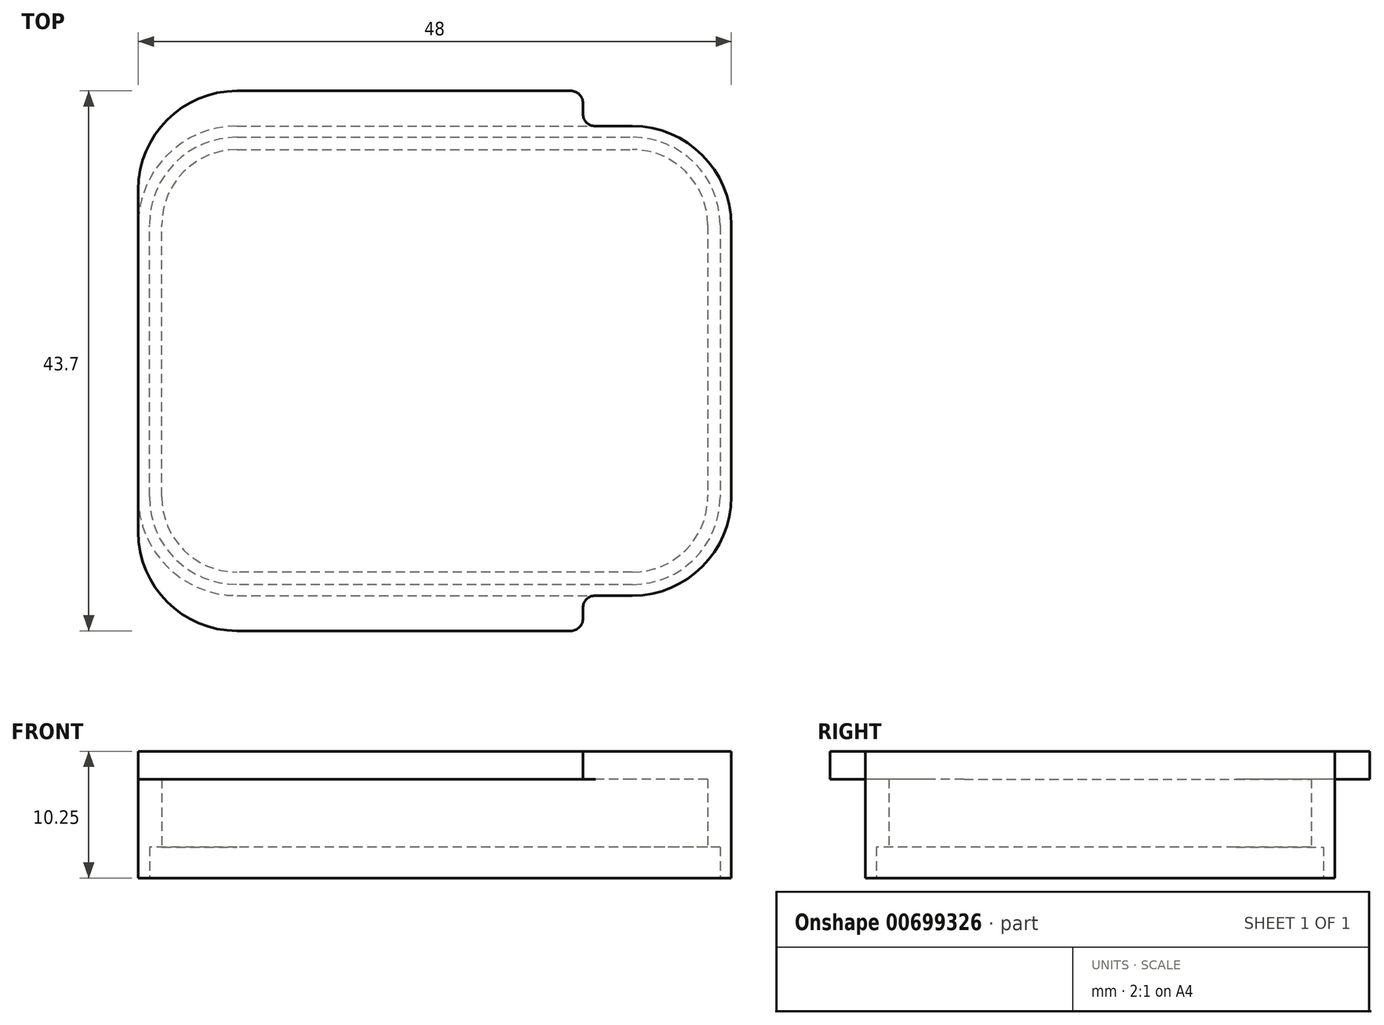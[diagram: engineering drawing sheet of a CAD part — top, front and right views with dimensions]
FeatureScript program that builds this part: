
annotation { "Feature Type Name" : "Feature", "Feature Type Description" : "" }
export const myFeature = defineFeature(function(context is Context, id is Id, definition is map)
    precondition{}
    {
        {
            var Q0;
            Q0=qCreatedBy(makeId("Top.planeOp"),FACE);
            var sketch = newSketch(context, id + "F0", { "sketchPlane" : qUnion([Q0])});
            skLineSegment(sketch, "E0.bottom", {"start": v(-16, 19) * mm, "end": v(16, 19) * mm});
            skLineSegment(sketch, "E0.top", {"start": v(-16, -19) * mm, "end": v(16, -19) * mm});
            skLineSegment(sketch, "E0.left", {"start": v(-24, 11) * mm, "end": v(-24, -11) * mm});
            skLineSegment(sketch, "E0.right", {"start": v(24, 11) * mm, "end": v(24, -11) * mm});
            skPoint(sketch, "E1.visualSharp", {"position": v(-24, 19) * mm});
            skArc(sketch, "E1.filletArc", {"start": v(-16, 19) * mm, "mid": v(-21.66, 16.66) * mm, "end": v(-24, 11) * mm});
            skPoint(sketch, "E2.visualSharp", {"position": v(24, 19) * mm});
            skArc(sketch, "E2.filletArc", {"start": v(24, 11) * mm, "mid": v(21.66, 16.66) * mm, "end": v(16, 19) * mm});
            skPoint(sketch, "E3.visualSharp", {"position": v(24, -19) * mm});
            skArc(sketch, "E3.filletArc", {"start": v(16, -19) * mm, "mid": v(21.66, -16.66) * mm, "end": v(24, -11) * mm});
            skPoint(sketch, "E4.visualSharp", {"position": v(-24, -19) * mm});
            skArc(sketch, "E4.filletArc", {"start": v(-24, -11) * mm, "mid": v(-21.66, -16.66) * mm, "end": v(-16, -19) * mm});
            skSolve(sketch);
        }
        {
            var Q0;
            Q0 = qSketchRegion(id + "F0", true);
            extrude(context, id + "F1", {"entities" : qUnion([Q0]), "depth" : 10.25 * mm, "offsetDistance" : 25 * mm});
        }
        {
            var Q0;
            Q0=makeQuery(id+"F1.opExtrude","CAP_FACE",FACE,{"disambiguationData":[OSD([sQuery(id+"F0.wireOp",EDGE,"E0.bottom"),sQuery(id+"F0.wireOp",EDGE,"E0.top"),sQuery(id+"F0.wireOp",EDGE,"E0.left"),sQuery(id+"F0.wireOp",EDGE,"E0.right"),sQuery(id+"F0.wireOp",EDGE,"E1.filletArc"),sQuery(id+"F0.wireOp",EDGE,"E2.filletArc"),sQuery(id+"F0.wireOp",EDGE,"E3.filletArc"),sQuery(id+"F0.wireOp",EDGE,"E4.filletArc")])],"isStart":false});
            var sketch = newSketch(context, id + "F2", { "sketchPlane" : qUnion([Q0])});
            skLineSegment(sketch, "E5.bottom", {"start": v(12, 21.85) * mm, "end": v(-24, 21.85) * mm});
            skLineSegment(sketch, "E5.top", {"start": v(12, -21.85) * mm, "end": v(-24, -21.85) * mm});
            skLineSegment(sketch, "E5.left", {"start": v(12, 21.85) * mm, "end": v(12, -21.85) * mm});
            skLineSegment(sketch, "E5.right", {"start": v(-24, 21.85) * mm, "end": v(-24, -21.85) * mm});
            skSolve(sketch);
        }
        {
            var Q0;
            Q0 = qSketchRegion(id + "F2", true);
            extrude(context, id + "F3", {"entities" : qUnion([Q0]), "operationType" : NewBodyOperationType.ADD, "oppositeDirection" : true, "depth" : 2.25 * mm, "offsetDistance" : 25 * mm});
        }
        {
            var Q0;
            Q0=makeQuery(id+"F3.opExtrude","SWEPT_EDGE",EDGE,{"disambiguationData":[OSD([sQuery(id+"F2.wireOp",EDGE,"E5.top"),sQuery(id+"F2.wireOp",EDGE,"E5.right")])]});
            var Q1;
            Q1=makeQuery(id+"F3.opExtrude","SWEPT_EDGE",EDGE,{"disambiguationData":[OSD([sQuery(id+"F2.wireOp",EDGE,"E5.bottom"),sQuery(id+"F2.wireOp",EDGE,"E5.right")])]});
            fillet(context, id + "F4", {"entities" : qUnion([Q0, Q1]), "radius" : 8 * mm, "tangentPropagation" : true, "allowEdgeOverflow" : false});
        }
        {
            var Q0;
            Q0=makeQuery(id+"F3.opExtrude","SWEPT_EDGE",EDGE,{"disambiguationData":[OSD([sQuery(id+"F2.wireOp",EDGE,"E5.top"),sQuery(id+"F2.wireOp",EDGE,"E5.left")])]});
            var Q1;
            Q1=makeQuery(id+"F3.opExtrude","SWEPT_EDGE",EDGE,{"disambiguationData":[OSD([sQuery(id+"F2.wireOp",EDGE,"E5.bottom"),sQuery(id+"F2.wireOp",EDGE,"E5.left")])]});
            fillet(context, id + "F5", {"entities" : qUnion([Q0, Q1]), "radius" : 1 * mm, "tangentPropagation" : true, "allowEdgeOverflow" : false});
        }
        {
            var Q0;
            Q0=makeQuery(id+"F3.boolean.opBoolean","INTERSECT",EDGE,{"derivedFrom":[makeQuery(id+"F1.opExtrude","SWEPT_FACE",FACE,{"disambiguationData":[OSD([sQuery(id+"F0.wireOp",EDGE,"E0.bottom")])]}),makeQuery(id+"F3.opExtrude","SWEPT_FACE",FACE,{"disambiguationData":[OSD([sQuery(id+"F2.wireOp",EDGE,"E5.left")])]})]});
            var Q1;
            Q1=makeQuery(id+"F3.boolean.opBoolean","INTERSECT",EDGE,{"derivedFrom":[makeQuery(id+"F1.opExtrude","SWEPT_FACE",FACE,{"disambiguationData":[OSD([sQuery(id+"F0.wireOp",EDGE,"E0.top")])]}),makeQuery(id+"F3.opExtrude","SWEPT_FACE",FACE,{"disambiguationData":[OSD([sQuery(id+"F2.wireOp",EDGE,"E5.left")])]})]});
            fillet(context, id + "F6", {"entities" : qUnion([Q0, Q1]), "radius" : 1 * mm, "tangentPropagation" : true, "allowEdgeOverflow" : false});
        }
        {
            var Q0;
            Q0=makeQuery(id+"F1.opExtrude","CAP_FACE",FACE,{"disambiguationData":[OSD([sQuery(id+"F0.wireOp",EDGE,"E0.bottom"),sQuery(id+"F0.wireOp",EDGE,"E0.top"),sQuery(id+"F0.wireOp",EDGE,"E0.left"),sQuery(id+"F0.wireOp",EDGE,"E0.right"),sQuery(id+"F0.wireOp",EDGE,"E1.filletArc"),sQuery(id+"F0.wireOp",EDGE,"E2.filletArc"),sQuery(id+"F0.wireOp",EDGE,"E3.filletArc"),sQuery(id+"F0.wireOp",EDGE,"E4.filletArc")])],"isStart":true});
            var sketch = newSketch(context, id + "F7", { "sketchPlane" : qUnion([Q0])});
            skArc(sketch, "E6.0.0", {"start": v(-16, 19) * mm, "mid": v(-21.66, 16.66) * mm, "end": v(-24, 11) * mm, "construction": true});
            skLineSegment(sketch, "E6.0.1", {"start": v(-24, 11) * mm, "end": v(-24, -11) * mm, "construction": true});
            skArc(sketch, "E6.0.2", {"start": v(-24, -11) * mm, "mid": v(-21.66, -16.66) * mm, "end": v(-16, -19) * mm, "construction": true});
            skLineSegment(sketch, "E6.0.3", {"start": v(-16, -19) * mm, "end": v(16, -19) * mm, "construction": true});
            skArc(sketch, "E6.0.4", {"start": v(16, -19) * mm, "mid": v(21.66, -16.66) * mm, "end": v(24, -11) * mm, "construction": true});
            skLineSegment(sketch, "E6.0.5", {"start": v(24, -11) * mm, "end": v(24, 11) * mm, "construction": true});
            skArc(sketch, "E6.0.6", {"start": v(24, 11) * mm, "mid": v(21.66, 16.66) * mm, "end": v(16, 19) * mm, "construction": true});
            skLineSegment(sketch, "E6.0.7", {"start": v(16, 19) * mm, "end": v(-16, 19) * mm, "construction": true});
            skArc(sketch, "E7.0", {"start": v(23.1, 11) * mm, "mid": v(21.02, 16.02) * mm, "end": v(16, 18.1) * mm});
            skLineSegment(sketch, "E7.1", {"start": v(23.1, -11) * mm, "end": v(23.1, 11) * mm});
            skLineSegment(sketch, "E7.2", {"start": v(16, 18.1) * mm, "end": v(-16, 18.1) * mm});
            skArc(sketch, "E7.3", {"start": v(16, -18.1) * mm, "mid": v(21.02, -16.02) * mm, "end": v(23.1, -11) * mm});
            skArc(sketch, "E7.4", {"start": v(-16, 18.1) * mm, "mid": v(-21.02, 16.02) * mm, "end": v(-23.1, 11) * mm});
            skLineSegment(sketch, "E7.5", {"start": v(-23.1, 11) * mm, "end": v(-23.1, -11) * mm});
            skArc(sketch, "E7.6", {"start": v(-23.1, -11) * mm, "mid": v(-21.02, -16.02) * mm, "end": v(-16, -18.1) * mm});
            skLineSegment(sketch, "E7.7", {"start": v(-16, -18.1) * mm, "end": v(16, -18.1) * mm});
            skLineSegment(sketch, "E8.0", {"start": v(16, 17.1) * mm, "end": v(-16, 17.1) * mm});
            skArc(sketch, "E8.1", {"start": v(22.1, 11) * mm, "mid": v(20.31, 15.31) * mm, "end": v(16, 17.1) * mm});
            skArc(sketch, "E8.2", {"start": v(-16, 17.1) * mm, "mid": v(-20.31, 15.31) * mm, "end": v(-22.1, 11) * mm});
            skLineSegment(sketch, "E8.3", {"start": v(22.1, -11) * mm, "end": v(22.1, 11) * mm});
            skLineSegment(sketch, "E8.4", {"start": v(-22.1, 11) * mm, "end": v(-22.1, -11) * mm});
            skArc(sketch, "E8.5", {"start": v(-22.1, -11) * mm, "mid": v(-20.31, -15.31) * mm, "end": v(-16, -17.1) * mm});
            skLineSegment(sketch, "E8.6", {"start": v(-16, -17.1) * mm, "end": v(16, -17.1) * mm});
            skArc(sketch, "E8.7", {"start": v(16, -17.1) * mm, "mid": v(20.31, -15.31) * mm, "end": v(22.1, -11) * mm});
            skSolve(sketch);
        }
        {
            var Q0;
            Q0=makeQuery(id+"F7.imprint","IMPRINT",FACE,{"disambiguationData":[TD([[makeQuery(id+"F7.imprint","IMPRINT",EDGE,{"derivedFrom":sQuery(id+"F7.wireOp",EDGE,"E8.0")}),1.0]])]});
            extrude(context, id + "F8", {"entities" : qUnion([Q0]), "operationType" : NewBodyOperationType.REMOVE, "oppositeDirection" : true, "depth" : 8 * mm, "offsetDistance" : 25 * mm});
        }
        {
            var Q0;
            Q0=makeQuery(id+"F7.imprint","IMPRINT",FACE,{"disambiguationData":[TD([[makeQuery(id+"F7.imprint","IMPRINT",EDGE,{"derivedFrom":sQuery(id+"F7.wireOp",EDGE,"E7.0")}),1.0]])]});
            extrude(context, id + "F9", {"entities" : qUnion([Q0]), "operationType" : NewBodyOperationType.REMOVE, "oppositeDirection" : true, "depth" : 2.5 * mm, "offsetDistance" : 25 * mm});
        }
    });
